# Revit family: SOLCRAFTE_PLUS200-SO31463
name_source: partatom
category: Aparatos eléctricos
revit_build: Autodesk Revit 2016 (Build: 20150220_1215(x64)
units: mm (PartAtom-declared; Revit-internal decimal feet)

## family parameters
Compartido = No
Corte con vacíos al cargar = No
Cota de conector redondo = Diámetro de uso
Mantener orientación de anotación = No
Número OmniClass = 23.80.00.00
Punto de cálculo de habitación = No
Se basa en plano de trabajo = No
Siempre vertical = Sí
Tipo de pieza = Caja de conexiones
Título OmniClass = Electric Power and Lighting

## types (2) — shared parameters
Aislamiento = 30 mm espuma PU
Altura = 212 mm
Conexiones = 2 x3/4" conexiones macho
Descripción = CAPTADOR SOLAR CON ACUMULADOR
Fabricante = SALVADOR ESCODA
Imagen de tipo = Solcrafte_Plus.jpg
Instalación = cubierta plana / cubierta inclinada
Longitud = 2184 mm
Pres. máx. de trabajo = 4 bar
Resistencia elec. opcional = 1 kW
Temp. máx. trabajo = 95 ºC
URL = www.salvadorescoda.com
zero-valued in all types: Costo

## per-type parameters (varying)
| type | Anchura | Capacidad | Certificación ministerio | Código de montaje | Modelo | Peso (vacio, sin elem. fij.) | Superfície total captador |
| SOLCRAFTE PLUS 150 | 800 mm | 145 l | SS-15513 | SO31462 | SOLCRAFTE PLUS 150L | 60 Kg | 1.75 m2 |
| SOLCRAFTE PLUS 200 | 1100 mm | 195 l | SS-15613 | SO31463 | SOLCRAFTE PLUS 200L | 75 Kg | 2.4 m2 |
